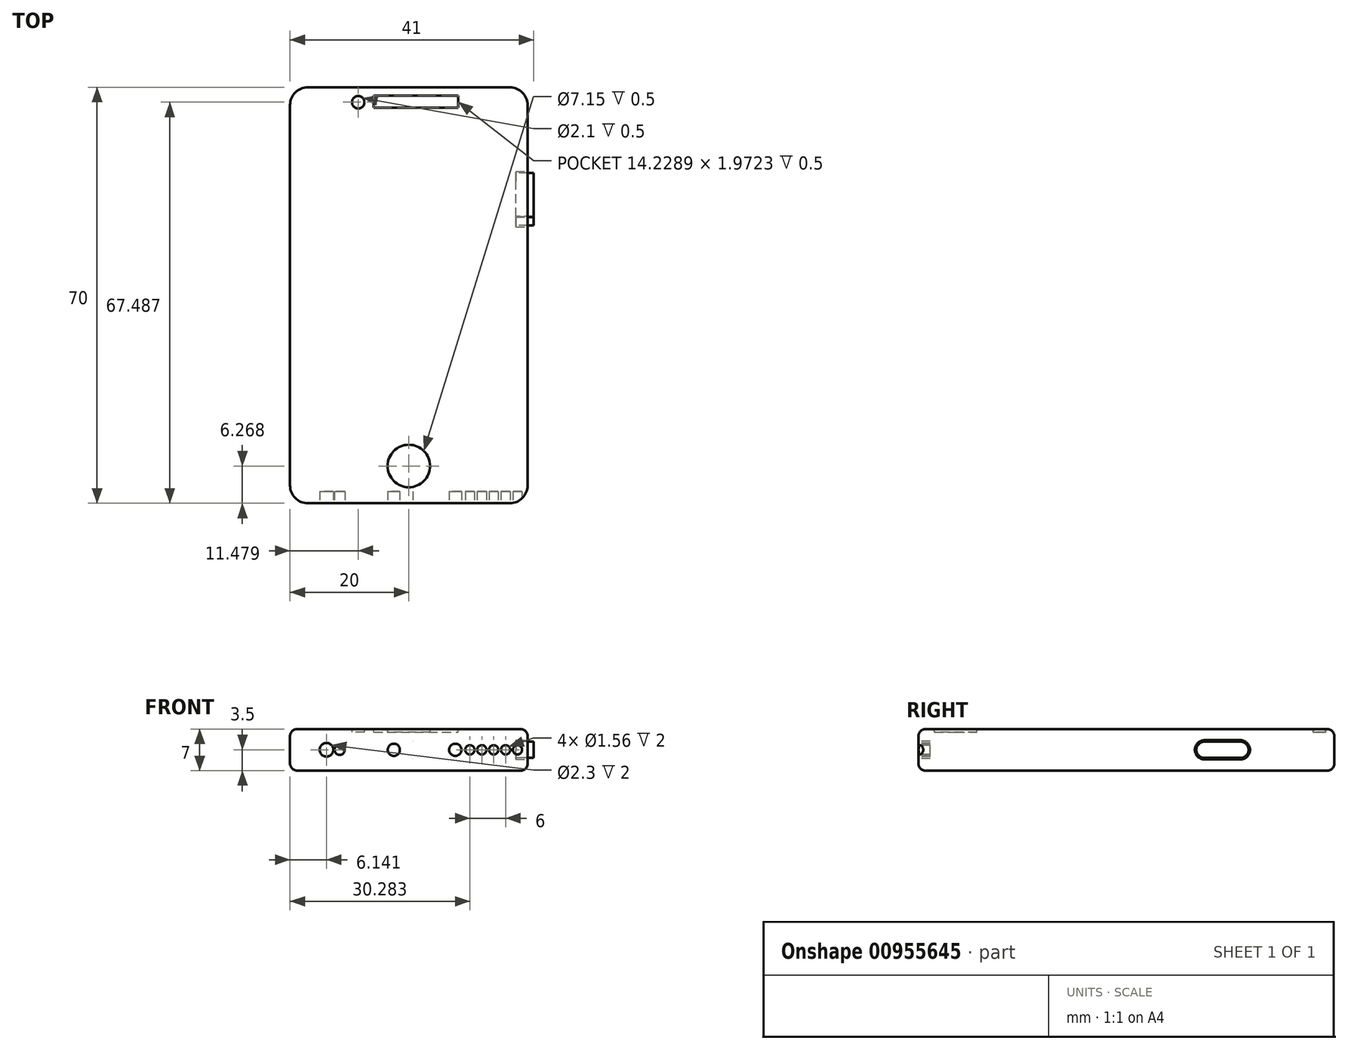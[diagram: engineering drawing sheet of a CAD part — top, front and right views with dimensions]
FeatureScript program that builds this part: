
annotation { "Feature Type Name" : "Feature", "Feature Type Description" : "" }
export const myFeature = defineFeature(function(context is Context, id is Id, definition is map)
    precondition{}
    {
        {
            var Q0;
            Q0=qCreatedBy(makeId("Top.planeOp"),FACE);
            var sketch = newSketch(context, id + "F0", { "sketchPlane" : qUnion([Q0])});
            skLineSegment(sketch, "E0.bottom", {"start": v(0, 70) * mm, "end": v(40, 70) * mm});
            skLineSegment(sketch, "E0.top", {"start": v(0, 0) * mm, "end": v(40, 0) * mm});
            skLineSegment(sketch, "E0.left", {"start": v(0, 70) * mm, "end": v(0, 0) * mm});
            skLineSegment(sketch, "E0.right", {"start": v(40, 70) * mm, "end": v(40, 0) * mm});
            skSolve(sketch);
        }
        {
            var Q0;
            Q0=makeQuery(id+"F0.imprint","IMPRINT",FACE,{"disambiguationData":[TD([[makeQuery(id+"F0.imprint","IMPRINT",EDGE,{"derivedFrom":sQuery(id+"F0.wireOp",EDGE,"E0.bottom")}),-1.0]])]});
            extrude(context, id + "F1", {"entities" : qUnion([Q0]), "depth" : 7 * mm, "offsetDistance" : 25 * mm});
        }
        {
            var Q0;
            Q0=makeQuery(id+"F1.opExtrude","SWEPT_FACE",FACE,{"disambiguationData":[OSD([sQuery(id+"F0.wireOp",EDGE,"E0.top")])]});
            var sketch = newSketch(context, id + "F2", { "sketchPlane" : qUnion([Q0])});
            skCircle(sketch, "E1", {"center": v(6.14, 3.5) * mm, "radius": 1.15 * mm});
            skPoint(sketch, "E1.centerSnap0", {"position": v(0, 3.5) * mm});
            skCircle(sketch, "E2", {"center": v(8.36, 3.5) * mm, "radius": 0.87 * mm});
            skCircle(sketch, "E3", {"center": v(17.47, 3.5) * mm, "radius": 1.02 * mm});
            skArc(sketch, "E4", {"start": v(20.7, 4.96) * mm, "mid": v(19.21, 3.5) * mm, "end": v(20.7, 2.04) * mm});
            skArc(sketch, "E5", {"start": v(24.76, 2.08) * mm, "mid": v(26.16, 3.5) * mm, "end": v(24.76, 4.92) * mm});
            skCircle(sketch, "E6", {"center": v(27.82, 3.5) * mm, "radius": 1.03 * mm});
            skCircle(sketch, "E7", {"center": v(30.28, 3.5) * mm, "radius": 0.78 * mm});
            skLineSegment(sketch, "E8", {"start": v(20.68, 4.96) * mm, "end": v(24.76, 4.92) * mm});
            skLineSegment(sketch, "E9", {"start": v(20.68, 2.04) * mm, "end": v(24.76, 2.08) * mm});
            skCircle(sketch, "E10.1.0.0", {"center": v(32.28, 3.5) * mm, "radius": 0.78 * mm});
            skCircle(sketch, "E10.2.0.0", {"center": v(34.28, 3.5) * mm, "radius": 0.78 * mm});
            skCircle(sketch, "E10.3.0.0", {"center": v(36.28, 3.5) * mm, "radius": 0.78 * mm});
            skCircle(sketch, "E10.4.0.0", {"center": v(38.28, 3.5) * mm, "radius": 0.78 * mm});
            skLineSegment(sketch, "E10.direction1", {"start": v(30.28, 3.5) * mm, "end": v(32.28, 3.5) * mm, "construction": true});
            skSolve(sketch);
        }
        {
            var Q0;
            Q0=makeQuery(id+"F2.imprint","IMPRINT",FACE,{"disambiguationData":[TD([[makeQuery(id+"F2.imprint","IMPRINT",EDGE,{"derivedFrom":sQuery(id+"F2.wireOp",EDGE,"E7")}),1.0]])]});
            var Q1;
            Q1=makeQuery(id+"F2.imprint","IMPRINT",FACE,{"disambiguationData":[TD([[makeQuery(id+"F2.imprint","IMPRINT",EDGE,{"derivedFrom":sQuery(id+"F2.wireOp",EDGE,"E3")}),1.0]])]});
            var Q2;
            Q2=makeQuery(id+"F2.imprint","IMPRINT",FACE,{"disambiguationData":[TD([[makeQuery(id+"F2.imprint","IMPRINT",EDGE,{"derivedFrom":sQuery(id+"F2.wireOp",EDGE,"E6")}),1.0]])]});
            var Q3;
            Q3=makeQuery(id+"F2.imprint","IMPRINT",FACE,{"disambiguationData":[TD([[makeQuery(id+"F2.imprint","IMPRINT",EDGE,{"derivedFrom":sQuery(id+"F2.wireOp",EDGE,"E10.4.0.0")}),1.0]])]});
            var Q4;
            Q4=makeQuery(id+"F2.imprint","IMPRINT",FACE,{"disambiguationData":[TD([[makeQuery(id+"F2.imprint","IMPRINT",EDGE,{"derivedFrom":sQuery(id+"F2.wireOp",EDGE,"E2")}),1.0]])]});
            var Q5;
            Q5=makeQuery(id+"F2.imprint","IMPRINT",FACE,{"disambiguationData":[TD([[makeQuery(id+"F2.imprint","IMPRINT",EDGE,{"derivedFrom":sQuery(id+"F2.wireOp",EDGE,"E10.3.0.0")}),1.0]])]});
            var Q6;
            Q6=makeQuery(id+"F2.imprint","IMPRINT",FACE,{"disambiguationData":[TD([[makeQuery(id+"F2.imprint","IMPRINT",EDGE,{"derivedFrom":sQuery(id+"F2.wireOp",EDGE,"E10.2.0.0")}),1.0]])]});
            var Q7;
            Q7=makeQuery(id+"F2.imprint","IMPRINT",FACE,{"disambiguationData":[TD([[makeQuery(id+"F2.imprint","IMPRINT",EDGE,{"derivedFrom":sQuery(id+"F2.wireOp",EDGE,"E10.1.0.0")}),1.0]])]});
            var Q8;
            {var subQ1=sQuery(id+"F2.wireOp",EDGE,"E4");Q8=makeQuery(id+"F2.imprint","IMPRINT",FACE,{"disambiguationData":[TD([[makeQuery(id+"F2.imprint","IMPRINT",EDGE,{"derivedFrom":subQ1}),1.0]])]});}
            var Q9;
            Q9=makeQuery(id+"F2.imprint","IMPRINT",FACE,{"disambiguationData":[TD([[makeQuery(id+"F2.imprint","IMPRINT",EDGE,{"derivedFrom":sQuery(id+"F2.wireOp",EDGE,"E1")}),1.0]])]});
            extrude(context, id + "F3", {"entities" : qUnion([Q0, Q1, Q2, Q3, Q4, Q5, Q6, Q7, Q8, Q9]), "operationType" : NewBodyOperationType.REMOVE, "oppositeDirection" : true, "depth" : 2 * mm, "offsetDistance" : 25 * mm});
        }
        {
            var Q0;
            Q0=makeQuery(id+"F1.opExtrude","SWEPT_FACE",FACE,{"disambiguationData":[OSD([sQuery(id+"F0.wireOp",EDGE,"E0.right")])]});
            var sketch = newSketch(context, id + "F4", { "sketchPlane" : qUnion([Q0])});
            skArc(sketch, "E11", {"start": v(48.17, 5.1) * mm, "mid": v(46.53, 3.46) * mm, "end": v(48.25, 1.9) * mm});
            skPoint(sketch, "E11.centerSnap0", {"position": v(0, 3.5) * mm});
            skArc(sketch, "E12", {"start": v(54.18, 1.88) * mm, "mid": v(55.8, 3.5) * mm, "end": v(54.18, 5.12) * mm});
            skLineSegment(sketch, "E13", {"start": v(48.17, 5.1) * mm, "end": v(54.18, 5.12) * mm});
            skLineSegment(sketch, "E14", {"start": v(48.25, 1.9) * mm, "end": v(54.18, 1.88) * mm});
            skSolve(sketch);
        }
        {
            var Q0;
            Q0=makeQuery(id+"F4.imprint","IMPRINT",FACE,{"disambiguationData":[TD([[makeQuery(id+"F4.imprint","IMPRINT",EDGE,{"derivedFrom":sQuery(id+"F4.wireOp",EDGE,"E11")}),1.0]])]});
            extrude(context, id + "F5", {"entities" : qUnion([Q0]), "operationType" : NewBodyOperationType.REMOVE, "oppositeDirection" : true, "depth" : 2 * mm, "offsetDistance" : 25 * mm});
        }
        {
            var Q0;
            Q0=makeQuery(id+"F5.boolean.opBoolean","COPY",FACE,{"derivedFrom":makeQuery(id+"F5.opExtrude","CAP_FACE",FACE,{"disambiguationData":[OSD([sQuery(id+"F4.wireOp",EDGE,"E11"),sQuery(id+"F4.wireOp",EDGE,"E12"),sQuery(id+"F4.wireOp",EDGE,"E13"),sQuery(id+"F4.wireOp",EDGE,"E14")])],"isStart":false})});
            var sketch = newSketch(context, id + "F6", { "sketchPlane" : qUnion([Q0])});
            skArc(sketch, "E15", {"start": v(48.17, 4.86) * mm, "mid": v(46.77, 3.46) * mm, "end": v(48.25, 2.14) * mm});
            skArc(sketch, "E16", {"start": v(54.18, 2.12) * mm, "mid": v(55.56, 3.5) * mm, "end": v(54.18, 4.88) * mm});
            skLineSegment(sketch, "E17", {"start": v(48.17, 4.86) * mm, "end": v(54.18, 4.88) * mm});
            skLineSegment(sketch, "E18", {"start": v(48.25, 2.14) * mm, "end": v(54.18, 2.12) * mm});
            skSolve(sketch);
        }
        {
            var Q0;
            Q0 = qSketchRegion(id + "F6", true);
            extrude(context, id + "F7", {"entities" : qUnion([Q0]), "operationType" : NewBodyOperationType.ADD, "depth" : 3 * mm, "offsetDistance" : 25 * mm});
        }
        {
            var Q0;
            Q0=makeQuery(id+"F1.opExtrude","CAP_FACE",FACE,{"disambiguationData":[OSD([sQuery(id+"F0.wireOp",EDGE,"E0.bottom"),sQuery(id+"F0.wireOp",EDGE,"E0.top"),sQuery(id+"F0.wireOp",EDGE,"E0.left"),sQuery(id+"F0.wireOp",EDGE,"E0.right")])],"isStart":false});
            var sketch = newSketch(context, id + "F8", { "sketchPlane" : qUnion([Q0])});
            skCircle(sketch, "E19", {"center": v(20, 6.27) * mm, "radius": 3.57 * mm});
            skPoint(sketch, "E19.centerSnap0", {"position": v(20, 0) * mm});
            skSolve(sketch);
        }
        {
            var Q0;
            Q0=makeQuery(id+"F8.imprint","IMPRINT",FACE,{"disambiguationData":[TD([[makeQuery(id+"F8.imprint","IMPRINT",EDGE,{"derivedFrom":sQuery(id+"F8.wireOp",EDGE,"E19")}),1.0]])]});
            var Q1;
            Q1=sQuery(id+"F8.wireOp",EDGE,"E19");
            extrude(context, id + "F9", {"entities" : qUnion([Q0]), "operationType" : NewBodyOperationType.REMOVE, "surfaceEntities" : qUnion([Q1]), "oppositeDirection" : true, "depth" : 0.5 * mm, "offsetDistance" : 25 * mm});
        }
        {
            var Q0;
            Q0=makeQuery(id+"F1.opExtrude","CAP_FACE",FACE,{"disambiguationData":[OSD([sQuery(id+"F0.wireOp",EDGE,"E0.bottom"),sQuery(id+"F0.wireOp",EDGE,"E0.top"),sQuery(id+"F0.wireOp",EDGE,"E0.left"),sQuery(id+"F0.wireOp",EDGE,"E0.right")])],"isStart":false});
            var sketch = newSketch(context, id + "F10", { "sketchPlane" : qUnion([Q0])});
            skCircle(sketch, "E20", {"center": v(11.48, 67.49) * mm, "radius": 1.05 * mm});
            skLineSegment(sketch, "E21.bottom", {"start": v(14.1, 68.57) * mm, "end": v(28.32, 68.57) * mm});
            skLineSegment(sketch, "E21.top", {"start": v(14.1, 66.6) * mm, "end": v(28.32, 66.6) * mm});
            skLineSegment(sketch, "E21.left", {"start": v(14.1, 68.57) * mm, "end": v(14.1, 66.6) * mm});
            skLineSegment(sketch, "E21.right", {"start": v(28.32, 68.57) * mm, "end": v(28.32, 66.6) * mm});
            skSolve(sketch);
        }
        {
            var Q0;
            Q0=makeQuery(id+"F10.imprint","IMPRINT",FACE,{"disambiguationData":[TD([[makeQuery(id+"F10.imprint","IMPRINT",EDGE,{"derivedFrom":sQuery(id+"F10.wireOp",EDGE,"E21.bottom")}),-1.0]])]});
            var Q1;
            Q1=makeQuery(id+"F10.imprint","IMPRINT",FACE,{"disambiguationData":[TD([[makeQuery(id+"F10.imprint","IMPRINT",EDGE,{"derivedFrom":sQuery(id+"F10.wireOp",EDGE,"E20")}),1.0]])]});
            extrude(context, id + "F11", {"entities" : qUnion([Q0, Q1]), "operationType" : NewBodyOperationType.REMOVE, "oppositeDirection" : true, "depth" : 0.5 * mm, "offsetDistance" : 25 * mm});
        }
        {
            var Q0;
            Q0=makeQuery(id+"F1.opExtrude","SWEPT_EDGE",EDGE,{"disambiguationData":[OSD([sQuery(id+"F0.wireOp",EDGE,"E0.bottom"),sQuery(id+"F0.wireOp",EDGE,"E0.right")])]});
            var Q1;
            Q1=makeQuery(id+"F1.opExtrude","SWEPT_EDGE",EDGE,{"disambiguationData":[OSD([sQuery(id+"F0.wireOp",EDGE,"E0.bottom"),sQuery(id+"F0.wireOp",EDGE,"E0.left")])]});
            var Q2;
            Q2=makeQuery(id+"F1.opExtrude","SWEPT_EDGE",EDGE,{"disambiguationData":[OSD([sQuery(id+"F0.wireOp",EDGE,"E0.top"),sQuery(id+"F0.wireOp",EDGE,"E0.left")])]});
            var Q3;
            Q3=makeQuery(id+"F1.opExtrude","SWEPT_EDGE",EDGE,{"disambiguationData":[OSD([sQuery(id+"F0.wireOp",EDGE,"E0.top"),sQuery(id+"F0.wireOp",EDGE,"E0.right")])]});
            fillet(context, id + "F12", {"entities" : qUnion([Q0, Q1, Q2, Q3]), "radius" : 3 * mm, "tangentPropagation" : true, "allowEdgeOverflow" : false});
        }
        {
            var Q0;
            Q0=makeQuery(id+"F1.opExtrude","CAP_EDGE",EDGE,{"disambiguationData":[OSD([sQuery(id+"F0.wireOp",EDGE,"E0.right")])],"isStart":false});
            fillet(context, id + "F13", {"entities" : qUnion([Q0]), "radius" : 1.2 * mm, "tangentPropagation" : true, "allowEdgeOverflow" : false});
        }
        {
            var Q0;
            Q0=makeQuery(id+"F1.opExtrude","CAP_EDGE",EDGE,{"disambiguationData":[OSD([sQuery(id+"F0.wireOp",EDGE,"E0.right")])],"isStart":true});
            fillet(context, id + "F14", {"entities" : qUnion([Q0]), "radius" : 1.2 * mm, "tangentPropagation" : true, "allowEdgeOverflow" : false});
        }
    });
